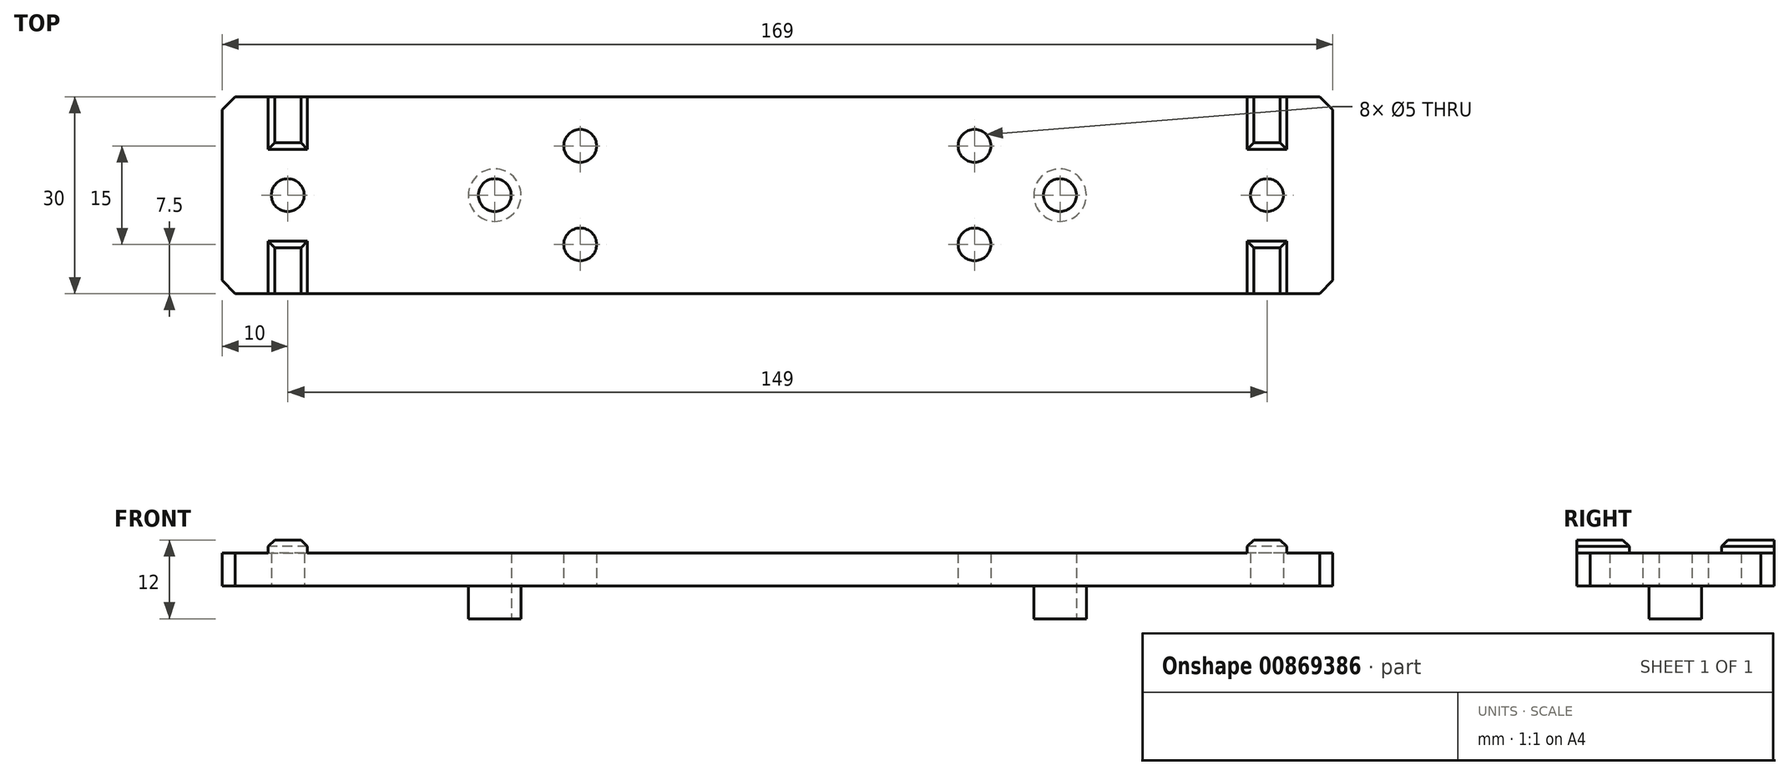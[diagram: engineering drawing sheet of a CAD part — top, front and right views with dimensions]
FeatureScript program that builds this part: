
annotation { "Feature Type Name" : "Feature", "Feature Type Description" : "" }
export const myFeature = defineFeature(function(context is Context, id is Id, definition is map)
    precondition{}
    {
        {
            var Q0;
            Q0=qCreatedBy(makeId("Top.planeOp"),FACE);
            var sketch = newSketch(context, id + "F0", { "sketchPlane" : qUnion([Q0])});
            skCircle(sketch, "E0", {"center": v(-43, 0) * mm, "radius": 2.5 * mm});
            skCircle(sketch, "E1", {"center": v(43, 0) * mm, "radius": 2.5 * mm});
            skCircle(sketch, "E2", {"center": v(-43, 0) * mm, "radius": 4 * mm});
            skCircle(sketch, "E3", {"center": v(43, 0) * mm, "radius": 4 * mm});
            skLineSegment(sketch, "E4.bottom", {"start": v(-84.5, 15) * mm, "end": v(84.5, 15) * mm});
            skLineSegment(sketch, "E4.top", {"start": v(-84.5, -15) * mm, "end": v(84.5, -15) * mm});
            skLineSegment(sketch, "E4.left", {"start": v(-84.5, 15) * mm, "end": v(-84.5, -15) * mm});
            skLineSegment(sketch, "E4.right", {"start": v(84.5, 15) * mm, "end": v(84.5, -15) * mm});
            skLineSegment(sketch, "E5.bottom", {"start": v(-77.5, 15) * mm, "end": v(-71.5, 15) * mm});
            skLineSegment(sketch, "E5.top", {"start": v(-77.5, 7) * mm, "end": v(-71.5, 7) * mm});
            skLineSegment(sketch, "E5.left", {"start": v(-77.5, 15) * mm, "end": v(-77.5, 7) * mm});
            skLineSegment(sketch, "E5.right", {"start": v(-71.5, 15) * mm, "end": v(-71.5, 7) * mm});
            skLineSegment(sketch, "E6.bottom", {"start": v(-77.5, -15) * mm, "end": v(-71.5, -15) * mm});
            skLineSegment(sketch, "E6.top", {"start": v(-77.5, -7) * mm, "end": v(-71.5, -7) * mm});
            skLineSegment(sketch, "E6.left", {"start": v(-77.5, -15) * mm, "end": v(-77.5, -7) * mm});
            skLineSegment(sketch, "E6.right", {"start": v(-71.5, -15) * mm, "end": v(-71.5, -7) * mm});
            skLineSegment(sketch, "E7.MirrorCS", {"start": v(71.5, 15) * mm, "end": v(71.5, 7) * mm});
            skLineSegment(sketch, "E8.MirrorCS", {"start": v(77.5, 7) * mm, "end": v(71.5, 7) * mm});
            skLineSegment(sketch, "E9.MirrorCS", {"start": v(77.5, 15) * mm, "end": v(77.5, 7) * mm});
            skLineSegment(sketch, "E10.MirrorCS", {"start": v(77.5, 15) * mm, "end": v(71.5, 15) * mm});
            skLineSegment(sketch, "E11.MirrorCS", {"start": v(77.5, -7) * mm, "end": v(71.5, -7) * mm});
            skLineSegment(sketch, "E12.MirrorCS", {"start": v(77.5, -15) * mm, "end": v(77.5, -7) * mm});
            skLineSegment(sketch, "E13.MirrorCS", {"start": v(71.5, -15) * mm, "end": v(71.5, -7) * mm});
            skLineSegment(sketch, "E14.MirrorCS", {"start": v(77.5, -15) * mm, "end": v(71.5, -15) * mm});
            skCircle(sketch, "E15", {"center": v(-74.5, 0) * mm, "radius": 2.5 * mm});
            skPoint(sketch, "E15.centerSnap0", {"position": v(-74.5, 7) * mm});
            skCircle(sketch, "E16.MirrorC", {"center": v(74.5, 0) * mm, "radius": 2.5 * mm});
            skCircle(sketch, "E17", {"center": v(-30, -7.5) * mm, "radius": 2.5 * mm});
            skCircle(sketch, "E18", {"center": v(30, -7.5) * mm, "radius": 2.5 * mm});
            skCircle(sketch, "E19.MirrorC", {"center": v(-30, 7.5) * mm, "radius": 2.5 * mm});
            skCircle(sketch, "E20.MirrorC", {"center": v(30, 7.5) * mm, "radius": 2.5 * mm});
            skSolve(sketch);
        }
        {
            var Q0;
            Q0=makeQuery(id+"F0.imprint","IMPRINT",FACE,{"disambiguationData":[TD([[makeQuery(id+"F0.imprint","IMPRINT",EDGE,{"derivedFrom":sQuery(id+"F0.wireOp",EDGE,"E2")}),-1.0]])]});
            var Q1;
            Q1=makeQuery(id+"F0.imprint","IMPRINT",FACE,{"disambiguationData":[TD([[makeQuery(id+"F0.imprint","IMPRINT",EDGE,{"derivedFrom":sQuery(id+"F0.wireOp",EDGE,"E0")}),-1.0]])]});
            var Q2;
            Q2=makeQuery(id+"F0.imprint","IMPRINT",FACE,{"disambiguationData":[TD([[makeQuery(id+"F0.imprint","IMPRINT",EDGE,{"derivedFrom":sQuery(id+"F0.wireOp",EDGE,"E1")}),-1.0]])]});
            extrude(context, id + "F1", {"entities" : qUnion([Q0, Q1, Q2]), "depth" : 5 * mm, "offsetDistance" : 25 * mm});
        }
        {
            var Q0;
            Q0=makeQuery(id+"F0.imprint","IMPRINT",FACE,{"disambiguationData":[TD([[makeQuery(id+"F0.imprint","IMPRINT",EDGE,{"derivedFrom":sQuery(id+"F0.wireOp",EDGE,"E5.top")}),1.0]])]});
            var Q1;
            Q1=makeQuery(id+"F0.imprint","IMPRINT",FACE,{"disambiguationData":[TD([[makeQuery(id+"F0.imprint","IMPRINT",EDGE,{"derivedFrom":sQuery(id+"F0.wireOp",EDGE,"E6.top")}),-1.0]])]});
            var Q2;
            Q2=makeQuery(id+"F0.imprint","IMPRINT",FACE,{"disambiguationData":[TD([[makeQuery(id+"F0.imprint","IMPRINT",EDGE,{"derivedFrom":sQuery(id+"F0.wireOp",EDGE,"E11.MirrorCS")}),1.0]])]});
            var Q3;
            {var subQ0=sQuery(id+"F0.wireOp",EDGE,"E7.MirrorCS");Q3=makeQuery(id+"F0.imprint","IMPRINT",FACE,{"disambiguationData":[TD([[makeQuery(id+"F0.imprint","IMPRINT",EDGE,{"derivedFrom":subQ0}),1.0]])]});}
            extrude(context, id + "F2", {"entities" : qUnion([Q0, Q1, Q2, Q3]), "operationType" : NewBodyOperationType.ADD, "depth" : 7 * mm, "offsetDistance" : 25 * mm});
        }
        {
            var Q0;
            Q0=makeQuery(id+"F2.opExtrude","CAP_EDGE",EDGE,{"disambiguationData":[OSD([sQuery(id+"F0.wireOp",EDGE,"E5.left")])],"isStart":false});
            var Q1;
            Q1=makeQuery(id+"F2.opExtrude","CAP_EDGE",EDGE,{"disambiguationData":[OSD([sQuery(id+"F0.wireOp",EDGE,"E5.right")])],"isStart":false});
            var Q2;
            Q2=makeQuery(id+"F2.opExtrude","CAP_EDGE",EDGE,{"disambiguationData":[OSD([sQuery(id+"F0.wireOp",EDGE,"E5.top")])],"isStart":false});
            var Q3;
            Q3=makeQuery(id+"F2.opExtrude","CAP_EDGE",EDGE,{"disambiguationData":[OSD([sQuery(id+"F0.wireOp",EDGE,"E6.top")])],"isStart":false});
            var Q4;
            Q4=makeQuery(id+"F2.opExtrude","CAP_EDGE",EDGE,{"disambiguationData":[OSD([sQuery(id+"F0.wireOp",EDGE,"E6.right")])],"isStart":false});
            var Q5;
            Q5=makeQuery(id+"F2.opExtrude","CAP_EDGE",EDGE,{"disambiguationData":[OSD([sQuery(id+"F0.wireOp",EDGE,"E6.left")])],"isStart":false});
            var Q6;
            Q6=makeQuery(id+"F2.opExtrude","CAP_EDGE",EDGE,{"disambiguationData":[OSD([sQuery(id+"F0.wireOp",EDGE,"E9.MirrorCS")])],"isStart":false});
            var Q7;
            Q7=makeQuery(id+"F2.opExtrude","CAP_EDGE",EDGE,{"disambiguationData":[OSD([sQuery(id+"F0.wireOp",EDGE,"E8.MirrorCS")])],"isStart":false});
            var Q8;
            Q8=makeQuery(id+"F2.opExtrude","CAP_EDGE",EDGE,{"disambiguationData":[OSD([sQuery(id+"F0.wireOp",EDGE,"E7.MirrorCS")])],"isStart":false});
            var Q9;
            Q9=makeQuery(id+"F2.opExtrude","CAP_EDGE",EDGE,{"disambiguationData":[OSD([sQuery(id+"F0.wireOp",EDGE,"E11.MirrorCS")])],"isStart":false});
            var Q10;
            Q10=makeQuery(id+"F2.opExtrude","CAP_EDGE",EDGE,{"disambiguationData":[OSD([sQuery(id+"F0.wireOp",EDGE,"E12.MirrorCS")])],"isStart":false});
            var Q11;
            Q11=makeQuery(id+"F2.opExtrude","CAP_EDGE",EDGE,{"disambiguationData":[OSD([sQuery(id+"F0.wireOp",EDGE,"E13.MirrorCS")])],"isStart":false});
            chamfer(context, id + "F3", {"entities" : qUnion([Q0, Q1, Q2, Q3, Q4, Q5, Q6, Q7, Q8, Q9, Q10, Q11]), "width" : 1 * mm, "tangentPropagation" : true});
        }
        {
            var Q0;
            Q0=makeQuery(id+"F0.imprint","IMPRINT",FACE,{"disambiguationData":[TD([[makeQuery(id+"F0.imprint","IMPRINT",EDGE,{"derivedFrom":sQuery(id+"F0.wireOp",EDGE,"E1")}),-1.0]])]});
            var Q1;
            Q1=makeQuery(id+"F0.imprint","IMPRINT",FACE,{"disambiguationData":[TD([[makeQuery(id+"F0.imprint","IMPRINT",EDGE,{"derivedFrom":sQuery(id+"F0.wireOp",EDGE,"E0")}),-1.0]])]});
            extrude(context, id + "F4", {"entities" : qUnion([Q0, Q1]), "operationType" : NewBodyOperationType.ADD, "oppositeDirection" : true, "depth" : 5 * mm, "offsetDistance" : 25 * mm});
        }
        {
            var Q0;
            Q0=makeQuery(id+"F1.opExtrude","SWEPT_EDGE",EDGE,{"disambiguationData":[OSD([sQuery(id+"F0.wireOp",EDGE,"E4.top"),sQuery(id+"F0.wireOp",EDGE,"E4.left")])]});
            var Q1;
            Q1=makeQuery(id+"F1.opExtrude","SWEPT_EDGE",EDGE,{"disambiguationData":[OSD([sQuery(id+"F0.wireOp",EDGE,"E4.bottom"),sQuery(id+"F0.wireOp",EDGE,"E4.left")])]});
            var Q2;
            Q2=makeQuery(id+"F1.opExtrude","SWEPT_EDGE",EDGE,{"disambiguationData":[OSD([sQuery(id+"F0.wireOp",EDGE,"E4.top"),sQuery(id+"F0.wireOp",EDGE,"E4.right")])]});
            var Q3;
            Q3=makeQuery(id+"F1.opExtrude","SWEPT_EDGE",EDGE,{"disambiguationData":[OSD([sQuery(id+"F0.wireOp",EDGE,"E4.bottom"),sQuery(id+"F0.wireOp",EDGE,"E4.right")])]});
            chamfer(context, id + "F5", {"entities" : qUnion([Q0, Q1, Q2, Q3]), "width" : 2 * mm, "tangentPropagation" : true});
        }
    });
